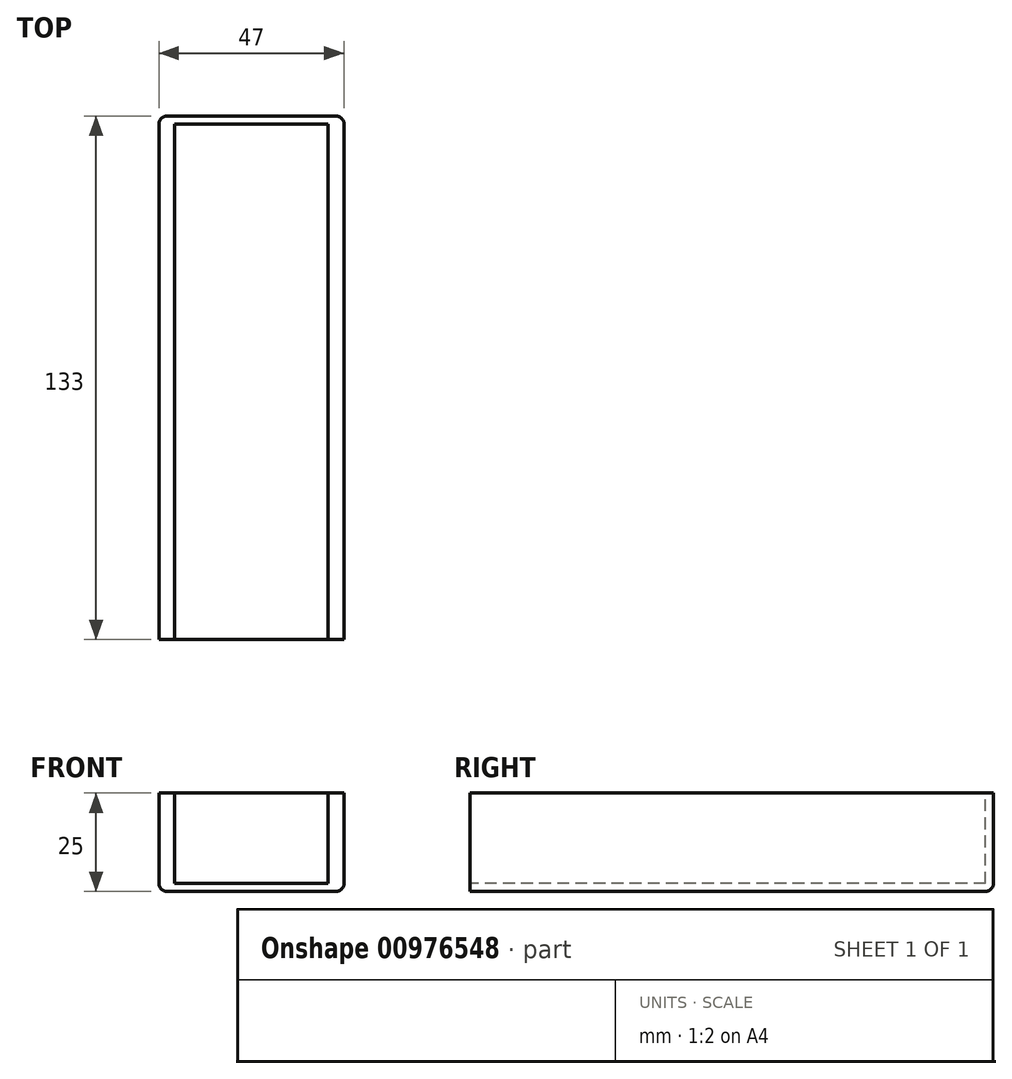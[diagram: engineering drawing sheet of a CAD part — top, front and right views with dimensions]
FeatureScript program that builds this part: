
annotation { "Feature Type Name" : "Feature", "Feature Type Description" : "" }
export const myFeature = defineFeature(function(context is Context, id is Id, definition is map)
    precondition{}
    {
        {
            var Q0;
            Q0=qCreatedBy(makeId("Top.planeOp"),FACE);
            var sketch = newSketch(context, id + "F0", { "sketchPlane" : qUnion([Q0])});
            skLineSegment(sketch, "E0.bottom", {"start": v(22.43, -49.59) * mm, "end": v(-24.57, -49.59) * mm});
            skLineSegment(sketch, "E0.top", {"start": v(22.43, 83.41) * mm, "end": v(-24.57, 83.41) * mm});
            skLineSegment(sketch, "E0.left", {"start": v(22.43, -49.59) * mm, "end": v(22.43, 83.41) * mm});
            skLineSegment(sketch, "E0.right", {"start": v(-24.57, -49.59) * mm, "end": v(-24.57, 83.41) * mm});
            skSolve(sketch);
        }
        {
            var Q0;
            Q0=makeQuery(id+"F0.imprint","IMPRINT",FACE,{"disambiguationData":[TD([[makeQuery(id+"F0.imprint","IMPRINT",EDGE,{"derivedFrom":sQuery(id+"F0.wireOp",EDGE,"E0.bottom")}),-1.0]])]});
            extrude(context, id + "F1", {"entities" : qUnion([Q0]), "depth" : 25 * mm, "offsetDistance" : 25 * mm});
        }
        {
            var Q0;
            Q0=makeQuery(id+"F1.opExtrude","SWEPT_FACE",FACE,{"disambiguationData":[OSD([sQuery(id+"F0.wireOp",EDGE,"E0.bottom")])]});
            var sketch = newSketch(context, id + "F2", { "sketchPlane" : qUnion([Q0])});
            skLineSegment(sketch, "E1.bottom", {"start": v(-21.57, 25) * mm, "end": v(19.43, 25) * mm});
            skLineSegment(sketch, "E1.top", {"start": v(-21.57, 2) * mm, "end": v(19.43, 2) * mm});
            skLineSegment(sketch, "E1.left", {"start": v(-21.57, 25) * mm, "end": v(-21.57, 2) * mm});
            skLineSegment(sketch, "E1.right", {"start": v(19.43, 25) * mm, "end": v(19.43, 2) * mm});
            skSolve(sketch);
        }
        {
            var Q0;
            Q0=makeQuery(id+"F2.imprint","IMPRINT",FACE,{"disambiguationData":[TD([[makeQuery(id+"F2.imprint","IMPRINT",EDGE,{"derivedFrom":sQuery(id+"F2.wireOp",EDGE,"E1.bottom")}),1.0]])]});
            var Q1;
            Q1=makeQuery(id+"F1.opExtrude","SWEPT_FACE",FACE,{"disambiguationData":[OSD([sQuery(id+"F0.wireOp",EDGE,"E0.top")])]});
            extrude(context, id + "F3", {"entities" : qUnion([Q0]), "operationType" : NewBodyOperationType.REMOVE, "endBound" : BoundingType.UP_TO_SURFACE, "oppositeDirection" : true, "depth" : 25 * mm, "endBoundEntityFace" : qUnion([Q1]), "hasOffset" : true, "offsetDistance" : 2 * mm});
        }
        {
            var Q0;
            Q0=makeQuery(id+"F1.opExtrude","CAP_EDGE",EDGE,{"disambiguationData":[OSD([sQuery(id+"F0.wireOp",EDGE,"E0.left")])],"isStart":true});
            var Q1;
            Q1=makeQuery(id+"F1.opExtrude","CAP_EDGE",EDGE,{"disambiguationData":[OSD([sQuery(id+"F0.wireOp",EDGE,"E0.top")])],"isStart":true});
            fillet(context, id + "F4", {"entities" : qUnion([Q0, Q1]), "radius" : 2 * mm, "tangentPropagation" : true, "allowEdgeOverflow" : false});
        }
        {
            var Q0;
            Q0=makeQuery(id+"F1.opExtrude","CAP_EDGE",EDGE,{"disambiguationData":[OSD([sQuery(id+"F0.wireOp",EDGE,"E0.right")])],"isStart":true});
            fillet(context, id + "F5", {"entities" : qUnion([Q0]), "radius" : 2 * mm, "tangentPropagation" : true, "allowEdgeOverflow" : false});
        }
        {
            var Q0;
            Q0=makeQuery(id+"F1.opExtrude","SWEPT_EDGE",EDGE,{"disambiguationData":[OSD([sQuery(id+"F0.wireOp",EDGE,"E0.top"),sQuery(id+"F0.wireOp",EDGE,"E0.left")])]});
            fillet(context, id + "F6", {"entities" : qUnion([Q0]), "radius" : 2 * mm, "tangentPropagation" : true, "allowEdgeOverflow" : false});
        }
        {
            var Q0;
            Q0=makeQuery(id+"F3.boolean.opBoolean","COPY",FACE,{"derivedFrom":makeQuery(id+"F3.opExtrude","SWEPT_FACE",FACE,{"disambiguationData":[OSD([sQuery(id+"F2.wireOp",EDGE,"E1.left")])]})});
            extrude(context, id + "F7", {"entities" : qUnion([Q0]), "operationType" : NewBodyOperationType.ADD, "depth" : 1 * mm, "offsetDistance" : 25 * mm});
        }
        {
            var Q0;
            Q0=makeQuery(id+"F3.boolean.opBoolean","COPY",FACE,{"derivedFrom":makeQuery(id+"F3.opExtrude","SWEPT_FACE",FACE,{"disambiguationData":[OSD([sQuery(id+"F2.wireOp",EDGE,"E1.right")])]})});
            extrude(context, id + "F8", {"entities" : qUnion([Q0]), "operationType" : NewBodyOperationType.ADD, "depth" : 1 * mm, "offsetDistance" : 25 * mm});
        }
        {
            var Q0;
            Q0=makeQuery(id+"F7.opExtrude","CAP_FACE",FACE,{"disambiguationData":[OSD([sQuery(id+"F2.wireOp",EDGE,"E1.left")])],"isStart":false});
            extrude(context, id + "F9", {"entities" : qUnion([Q0]), "operationType" : NewBodyOperationType.ADD, "oppositeDirection" : true, "depth" : 0.5 * mm, "offsetDistance" : 25 * mm});
        }
    });
